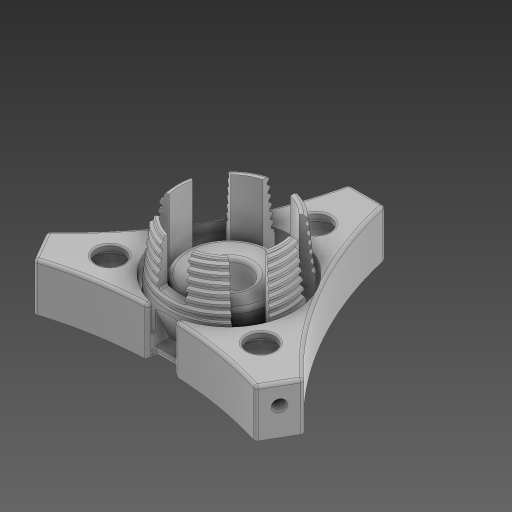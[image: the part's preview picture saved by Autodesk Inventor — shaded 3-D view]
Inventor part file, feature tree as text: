
AUTODESK INVENTOR PART (.ipt)
format: ipt  version: 2024 (Build 280153000, 153)  size: 1,674,752 bytes
history: native  units: mm
features: sketch x17, extrude x12, fillet x9, chamfer x3, hole x3, draft x2, helix x2, plane x2, pattern_circular x2, projected_geometry x2
ambient origin geometry x8: Origin, YZ Plane, XZ Plane, XY Plane, X Axis, Y Axis, Z Axis, Center Point
bodies: Solid1 (feature_tree)
feature tree (54):
  extrude  "Extrusion1"  Depth=29.5mm
  draft  "FaceDraft1"
  sketch  "Sketch2"  dims[d7=6.806784mm d8=0.55605mm]
  helix  "Coil1"  [1 undecoded]
  helix  "Coil2"  [1 undecoded]
  extrude  "Extrusion2"  Depth=0.55605mm
  extrude  "Extrusion3"  TaperAngle=0.0deg  [1 undecoded]
  fillet  "Fillet1"  [1 undecoded]
  chamfer  "Chamfer1"  Distance=0.3mm Angle=45.0deg
  plane  "Work Plane1"
  extrude  "Extrusion4"  TaperAngle=0.0deg  [1 undecoded]
  extrude  "Extrusion8"  Depth=60.0mm TaperAngle=360.0deg
  hole  "Hole2"  [1 undecoded]
  sketch  "Sketch13"  dims[d58=6.0mm d65=60.0mm d67=360.0deg]
  extrude  "Extrusion11"  Depth=10.0mm TaperAngle=0.0deg
  hole  "Hole4"  [1 undecoded]
  pattern_circular  "Circular Pattern4"  Count=3 Angle=360.0deg
  extrude  "Extrusion13"  Depth=7.0mm TaperAngle=0.0deg
  sketch  "Sketch20"  dims[d126=6.904mm d127=6.0mm d128=10.079mm d129=8.89mm d130=90.0deg d131=8.0mm d132=20.594885mm d133=22.0mm d134=30.0mm d135=360.0deg]
  extrude  "Extrusion14"  Depth=1.55mm TaperAngle=45.0deg
  sketch  "Sketch18"  dims[d124=34.0mm]
  fillet  "Fillet9"  Radius=0.24mm
  chamfer  "Chamfer4"  [1 undecoded]
  chamfer  "Chamfer5"  Distance=0.5mm
  fillet  "Fillet11"  Radius=2.0mm
  draft  "FaceDraft2"
  fillet  "Fillet13"  Radius=34.767mm
  extrude  "Extrusion15"  Depth=0.5mm
  hole  "Hole5"  [1 undecoded]
  pattern_circular  "Circular Pattern5"  [2 undecoded]
  plane  "Work Plane4"
  extrude  "Extrusion16"  Depth=0.5mm
  fillet  "Fillet14"  Radius=30.0mm
  fillet  "Fillet16"  Radius=16.0mm
  extrude  "Extrusion17"  TaperAngle=0.0deg  [1 undecoded]
  extrude  "Extrusion19"  Depth=0.5mm
  fillet  "Fillet17"  Radius=0.4mm
  fillet  "Fillet18"  Radius=25.0mm
  fillet  "Fillet19"  Radius=22.0mm
  sketch  "Sketch1"  dims[d0=25.0mm d1=29.5mm d2=12.875mm d3=0.0mm d4=1.047198mm]
  projected_geometry  "Projected Loop1"
  sketch  "Sketch3"  dims[d9=6.806784mm]
  sketch  "Sketch4"  dims[d10=2.0mm d11=10.0mm d12=70.0mm d13=-1.047198mm d14=90.0deg d15=90.0deg d16=0.0mm d17=0.0mm d18=0.6mm]
  sketch  "Sketch5"  dims[d19=2.0mm d20=10.0mm d21=10.0mm d22=1.047198mm d23=90.0deg d24=90.0deg d25=0.0mm d26=0.0mm d27=0.0mm d28=0.0mm d29=0.0mm d30=0.0mm]
  sketch  "Sketch10"  dims[d31=0.6mm d32=0.3mm d33=2.0mm d34=45.0deg]
  sketch  "Sketch11"  dims[d36=-2.0mm d42=0.0mm d43=0.0mm]
  sketch  "Sketch15"  dims[d91=33.0mm d92=12.0mm d93=0.0mm]
  sketch  "Sketch17"  dims[d94=5.3mm d95=6.0mm d96=10.0mm d97=7.0mm d98=90.0deg d99=8.0mm d100=20.594885mm d122=10.0mm d123=0.0mm]
  sketch  "Sketch21"  dims[d146=11.34464mm d147=7.0mm d148=0.0mm]
  sketch  "Sketch22"  dims[d150=1.0mm d151=1.55mm d152=2.0mm d153=45.0deg]
  sketch  "Sketch25"  dims[d154=0.5mm d155=2.0mm d156=45.0deg d158=0.24mm]
  sketch  "Sketch26"  dims[d160=1.25mm d161=0.0mm d162=0.0mm]
  sketch  "Sketch28"  dims[d163=30.0deg d164=0.5mm d165=2.0mm d166=34.767mm d167=9.0mm d168=30.0deg d169=7.0mm d170=0.0mm d171=3.0mm d172=6.0mm d173=9.779mm d174=7.62mm d175=90.0deg d176=7.0mm d177=0.0mm d178=5.0mm d179=30.0mm d180=360.0deg d182=16.0mm d183=0.0mm d184=0.0mm d185=0.75mm d187=0.4mm d188=25.0mm d189=22.0mm d190=31.0mm d191=7.0mm d192=0.0mm d193=32.8mm d208=9.0mm d209=0.0mm d210=1.0mm d211=0.25mm d212=0.5mm d213=7.0mm d214=60.0mm d216=360.0deg]
  projected_geometry  "Project Cut Edges3"
note: 12 required parameter values undecoded (feature->parameter linkage not recoverable at this tier; creation-order binding heuristic only, values carry confidence <= 0.55)
